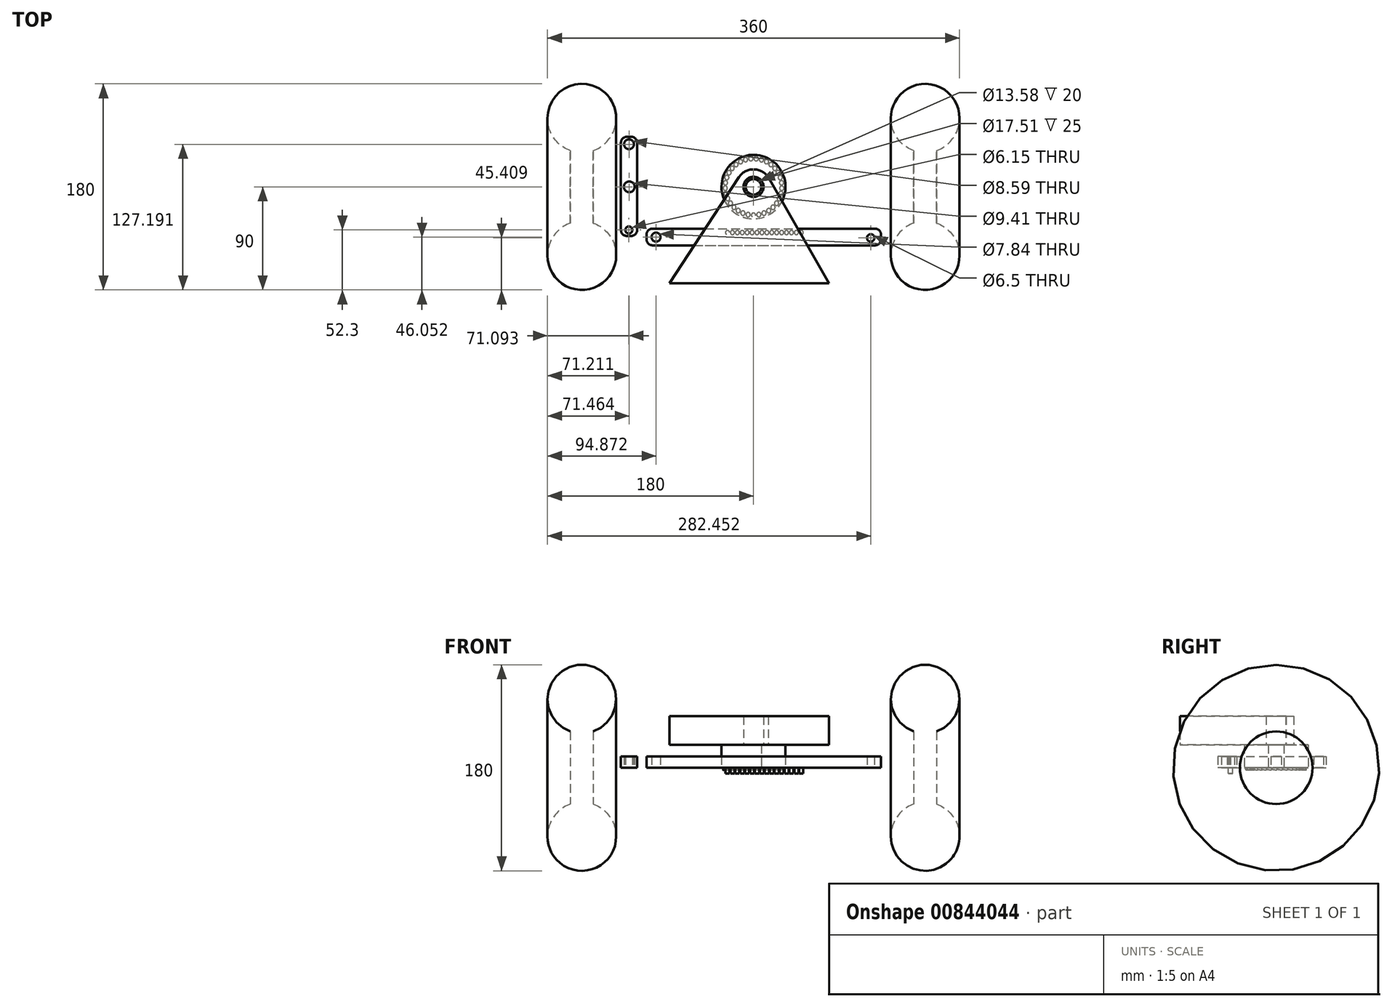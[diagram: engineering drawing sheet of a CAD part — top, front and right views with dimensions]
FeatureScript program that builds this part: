
annotation { "Feature Type Name" : "Feature", "Feature Type Description" : "" }
export const myFeature = defineFeature(function(context is Context, id is Id, definition is map)
    precondition{}
    {
        {
            var Q0;
            Q0=qCreatedBy(makeId("Front.planeOp"),FACE);
            var sketch = newSketch(context, id + "F0", { "sketchPlane" : qUnion([Q0])});
            skCircle(sketch, "E0", {"center": v(-150, 60) * mm, "radius": 30 * mm});
            skLineSegment(sketch, "E1.bottom", {"start": v(-160, 31.72) * mm, "end": v(-140, 31.72) * mm});
            skLineSegment(sketch, "E1.top", {"start": v(-160, 0) * mm, "end": v(-140, 0) * mm});
            skLineSegment(sketch, "E1.left", {"start": v(-140, 31.72) * mm, "end": v(-140, 0) * mm});
            skLineSegment(sketch, "E1.right", {"start": v(-160, 31.72) * mm, "end": v(-160, 0) * mm});
            skPoint(sketch, "E2.startSnap0", {"position": v(-150, 31.72) * mm});
            skLineSegment(sketch, "E3", {"start": v(-150, 31.72) * mm, "end": v(-150, 60) * mm});
            skLineSegment(sketch, "E4.MirrorCS", {"start": v(160, 31.72) * mm, "end": v(160, 0) * mm});
            skLineSegment(sketch, "E5.MirrorCS", {"start": v(140, 31.72) * mm, "end": v(140, 0) * mm});
            skPoint(sketch, "E6.MirrorP", {"position": v(150, 31.72) * mm});
            skLineSegment(sketch, "E7.MirrorCS", {"start": v(160, 31.72) * mm, "end": v(140, 31.72) * mm});
            skLineSegment(sketch, "E8.MirrorCS", {"start": v(160, 0) * mm, "end": v(140, 0) * mm});
            skCircle(sketch, "E9.MirrorC", {"center": v(150, 60) * mm, "radius": 30 * mm});
            skSolve(sketch);
        }
        {
            var Q0;
            Q0 = qSketchRegion(id + "F0", true);
            var Q1;
            Q1=sQuery(id+"F0.wireOp",EDGE,"E1.top");
            revolve(context, id + "F1", {"surfaceOperationType" : NewSurfaceOperationType.NEW, "entities" : qUnion([Q0]), "axis" : qUnion([Q1]), "revolveType" : RevolveType.FULL});
        }
        {
            var Q0;
            Q0=qCreatedBy(makeId("Top.planeOp"),FACE);
            var sketch = newSketch(context, id + "F2", { "sketchPlane" : qUnion([Q0])});
            skLineSegment(sketch, "E10.bottom", {"start": v(-110.82, -42.85) * mm, "end": v(-106.64, -42.85) * mm});
            skLineSegment(sketch, "E10.top", {"start": v(-110.82, 43.7) * mm, "end": v(-106.64, 43.7) * mm});
            skLineSegment(sketch, "E10.left", {"start": v(-115.82, -37.85) * mm, "end": v(-115.82, 38.7) * mm});
            skLineSegment(sketch, "E10.right", {"start": v(-101.64, -37.85) * mm, "end": v(-101.64, 38.7) * mm});
            skLineSegment(sketch, "E11.bottom", {"start": v(-88.44, -51.05) * mm, "end": v(106.34, -51.05) * mm});
            skLineSegment(sketch, "E11.top", {"start": v(-88.44, -36.5) * mm, "end": v(106.34, -36.5) * mm});
            skLineSegment(sketch, "E11.left", {"start": v(-93.44, -46.05) * mm, "end": v(-93.44, -41.5) * mm});
            skLineSegment(sketch, "E11.right", {"start": v(111.34, -46.05) * mm, "end": v(111.34, -41.5) * mm});
            skPoint(sketch, "E12.visualSharp", {"position": v(-93.44, -51.05) * mm});
            skArc(sketch, "E12.filletArc", {"start": v(-93.44, -46.05) * mm, "mid": v(-91.97, -49.59) * mm, "end": v(-88.44, -51.05) * mm});
            skPoint(sketch, "E13.visualSharp", {"position": v(-93.44, -36.5) * mm});
            skArc(sketch, "E13.filletArc", {"start": v(-88.44, -36.5) * mm, "mid": v(-91.97, -37.97) * mm, "end": v(-93.44, -41.5) * mm});
            skPoint(sketch, "E14.visualSharp", {"position": v(111.34, -51.05) * mm});
            skArc(sketch, "E14.filletArc", {"start": v(106.34, -51.05) * mm, "mid": v(109.88, -49.59) * mm, "end": v(111.34, -46.05) * mm});
            skPoint(sketch, "E15.visualSharp", {"position": v(111.34, -36.5) * mm});
            skArc(sketch, "E15.filletArc", {"start": v(111.34, -41.5) * mm, "mid": v(109.88, -37.97) * mm, "end": v(106.34, -36.5) * mm});
            skPoint(sketch, "E16.visualSharp", {"position": v(-101.64, -42.85) * mm});
            skArc(sketch, "E16.filletArc", {"start": v(-106.64, -42.85) * mm, "mid": v(-103.1, -41.38) * mm, "end": v(-101.64, -37.85) * mm});
            skPoint(sketch, "E17.visualSharp", {"position": v(-101.64, 43.7) * mm});
            skArc(sketch, "E17.filletArc", {"start": v(-101.64, 38.7) * mm, "mid": v(-103.1, 42.23) * mm, "end": v(-106.64, 43.7) * mm});
            skPoint(sketch, "E18.visualSharp", {"position": v(-115.82, 43.7) * mm});
            skArc(sketch, "E18.filletArc", {"start": v(-110.82, 43.7) * mm, "mid": v(-114.35, 42.23) * mm, "end": v(-115.82, 38.7) * mm});
            skPoint(sketch, "E19.visualSharp", {"position": v(-115.82, -42.85) * mm});
            skArc(sketch, "E19.filletArc", {"start": v(-115.82, -37.85) * mm, "mid": v(-114.35, -41.38) * mm, "end": v(-110.82, -42.85) * mm});
            skCircle(sketch, "E20", {"center": v(-85.13, -43.95) * mm, "radius": 3.92 * mm});
            skCircle(sketch, "E21", {"center": v(-108.9, -37.7) * mm, "radius": 3.08 * mm});
            skCircle(sketch, "E22", {"center": v(-108.79, 37.2) * mm, "radius": 4.3 * mm});
            skCircle(sketch, "E23", {"center": v(102.45, -44.6) * mm, "radius": 3.25 * mm});
            skCircle(sketch, "E24", {"center": v(-108.54, 0) * mm, "radius": 4.7 * mm});
            skSolve(sketch);
        }
        {
            var Q0;
            Q0 = qSketchRegion(id + "F2", true);
            extrude(context, id + "F3", {"entities" : qUnion([Q0]), "depth" : 10 * mm, "offsetDistance" : 25 * mm});
        }
        {
            var Q0;
            Q0=qCreatedBy(makeId("Top.planeOp"),FACE);
            var sketch = newSketch(context, id + "F4", { "sketchPlane" : qUnion([Q0])});
            skCircle(sketch, "E25", {"center": v(0, 0) * mm, "radius": 27.96 * mm});
            skCircle(sketch, "E26", {"center": v(0, 0) * mm, "radius": 6.79 * mm});
            skSolve(sketch);
        }
        {
            var Q0;
            Q0=makeQuery(id+"F4.imprint","IMPRINT",FACE,{"disambiguationData":[TD([[makeQuery(id+"F4.imprint","IMPRINT",EDGE,{"derivedFrom":sQuery(id+"F4.wireOp",EDGE,"E25")}),1.0]])]});
            extrude(context, id + "F5", {"entities" : qUnion([Q0]), "depth" : 20 * mm, "offsetDistance" : 25 * mm});
        }
        {
            var Q0;
            Q0=makeQuery(id+"F5.opExtrude","CAP_FACE",FACE,{"disambiguationData":[OSD([sQuery(id+"F4.wireOp",EDGE,"E25"),sQuery(id+"F4.wireOp",EDGE,"E26")])],"isStart":false});
            var sketch = newSketch(context, id + "F6", { "sketchPlane" : qUnion([Q0])});
            skLineSegment(sketch, "E27", {"start": v(-73.41, -84.14) * mm, "end": v(-12.8, 8.38) * mm});
            skLineSegment(sketch, "E28", {"start": v(12.8, 8.38) * mm, "end": v(66.1, -84.14) * mm});
            skArc(sketch, "E29", {"start": v(-12.8, 8.38) * mm, "mid": v(0, 15.3) * mm, "end": v(12.8, 8.38) * mm});
            skLineSegment(sketch, "E30", {"start": v(-73.41, -84.14) * mm, "end": v(66.1, -84.14) * mm});
            skCircle(sketch, "E31", {"center": v(0, 0) * mm, "radius": 8.76 * mm});
            skSolve(sketch);
        }
        {
            var Q0;
            Q0 = qSketchRegion(id + "F6", true);
            extrude(context, id + "F7", {"entities" : qUnion([Q0]), "operationType" : NewBodyOperationType.ADD, "depth" : 25 * mm, "offsetDistance" : 25 * mm});
        }
        {
            var Q0;
            Q0=makeQuery(id+"F5.opExtrude","CAP_FACE",FACE,{"disambiguationData":[OSD([sQuery(id+"F4.wireOp",EDGE,"E25"),sQuery(id+"F4.wireOp",EDGE,"E26")])],"isStart":true});
            var sketch = newSketch(context, id + "F8", { "sketchPlane" : qUnion([Q0])});
            skPoint(sketch, "E32.center", {"position": v(0, 0.62) * mm});
            skLineSegment(sketch, "E32.anchor1", {"start": v(0, 0.62) * mm, "end": v(0, 24.7) * mm, "construction": true});
            skPoint(sketch, "E33.center", {"position": v(8.35, 1.1) * mm});
            skCircle(sketch, "E34", {"center": v(0, 24.7) * mm, "radius": 1.9 * mm});
            skCircle(sketch, "E35.1.0", {"center": v(4.67, 24.26) * mm, "radius": 1.9 * mm});
            skCircle(sketch, "E35.2.0", {"center": v(9.18, 22.94) * mm, "radius": 1.9 * mm});
            skCircle(sketch, "E35.3.0", {"center": v(13.36, 20.79) * mm, "radius": 1.9 * mm});
            skCircle(sketch, "E35.4.0", {"center": v(17.05, 17.89) * mm, "radius": 1.9 * mm});
            skCircle(sketch, "E35.5.0", {"center": v(20.12, 14.34) * mm, "radius": 1.9 * mm});
            skCircle(sketch, "E35.6.0", {"center": v(22.47, 10.27) * mm, "radius": 1.9 * mm});
            skCircle(sketch, "E35.7.0", {"center": v(24.01, 5.83) * mm, "radius": 1.9 * mm});
            skCircle(sketch, "E35.8.0", {"center": v(24.68, 1.19) * mm, "radius": 1.9 * mm});
            skCircle(sketch, "E35.9.0", {"center": v(24.46, -3.5) * mm, "radius": 1.9 * mm});
            skCircle(sketch, "E35.10.0", {"center": v(23.35, -8.07) * mm, "radius": 1.9 * mm});
            skCircle(sketch, "E35.11.0", {"center": v(21.4, -12.34) * mm, "radius": 1.9 * mm});
            skCircle(sketch, "E35.12.0", {"center": v(18.68, -16.17) * mm, "radius": 1.9 * mm});
            skCircle(sketch, "E35.13.0", {"center": v(15.29, -19.41) * mm, "radius": 1.9 * mm});
            skCircle(sketch, "E35.14.0", {"center": v(11.34, -21.95) * mm, "radius": 1.9 * mm});
            skCircle(sketch, "E35.15.0", {"center": v(6.98, -23.7) * mm, "radius": 1.9 * mm});
            skCircle(sketch, "E35.16.0", {"center": v(2.37, -24.6) * mm, "radius": 1.9 * mm});
            skCircle(sketch, "E35.17.0", {"center": v(-2.33, -24.6) * mm, "radius": 1.9 * mm});
            skCircle(sketch, "E35.18.0", {"center": v(-6.94, -23.71) * mm, "radius": 1.9 * mm});
            skCircle(sketch, "E35.19.0", {"center": v(-11.3, -21.97) * mm, "radius": 1.9 * mm});
            skPoint(sketch, "E35.center", {"position": v(0, 0) * mm});
            skLineSegment(sketch, "E35.anchor1", {"start": v(0, 0) * mm, "end": v(0, 24.7) * mm, "construction": true});
            skLineSegment(sketch, "E35.anchor2", {"start": v(0, 0) * mm, "end": v(-4.71, 24.25) * mm, "construction": true});
            skCircle(sketch, "E36.1.20.0", {"center": v(-15.25, -19.44) * mm, "radius": 1.9 * mm});
            skCircle(sketch, "E37.1.21.0", {"center": v(-18.66, -16.2) * mm, "radius": 1.9 * mm});
            skCircle(sketch, "E38.1.22.0", {"center": v(-21.38, -12.38) * mm, "radius": 1.9 * mm});
            skCircle(sketch, "E39.1.23.0", {"center": v(-23.34, -8.1) * mm, "radius": 1.9 * mm});
            skCircle(sketch, "E40.1.24.0", {"center": v(-24.45, -3.55) * mm, "radius": 1.9 * mm});
            skCircle(sketch, "E41.1.25.0", {"center": v(-24.68, 1.15) * mm, "radius": 1.9 * mm});
            skCircle(sketch, "E42.1.26.0", {"center": v(-24.02, 5.8) * mm, "radius": 1.9 * mm});
            skCircle(sketch, "E43.1.27.0", {"center": v(-22.49, 10.23) * mm, "radius": 1.9 * mm});
            skCircle(sketch, "E44.1.28.0", {"center": v(-20.15, 14.3) * mm, "radius": 1.9 * mm});
            skCircle(sketch, "E45.1.29.0", {"center": v(-17.08, 17.86) * mm, "radius": 1.9 * mm});
            skCircle(sketch, "E46.1.30.0", {"center": v(-13.39, 20.77) * mm, "radius": 1.9 * mm});
            skCircle(sketch, "E47.1.31.0", {"center": v(-9.22, 22.92) * mm, "radius": 1.9 * mm});
            skCircle(sketch, "E48.1.32.0", {"center": v(-4.71, 24.25) * mm, "radius": 1.9 * mm});
            skSolve(sketch);
        }
        {
            var Q0;
            Q0=makeQuery(id+"F3.opExtrude","CAP_FACE",FACE,{"disambiguationData":[OSD([sQuery(id+"F2.wireOp",EDGE,"E11.bottom"),sQuery(id+"F2.wireOp",EDGE,"E11.top"),sQuery(id+"F2.wireOp",EDGE,"E11.left"),sQuery(id+"F2.wireOp",EDGE,"E11.right"),sQuery(id+"F2.wireOp",EDGE,"E12.filletArc"),sQuery(id+"F2.wireOp",EDGE,"E13.filletArc"),sQuery(id+"F2.wireOp",EDGE,"E14.filletArc"),sQuery(id+"F2.wireOp",EDGE,"E15.filletArc"),sQuery(id+"F2.wireOp",EDGE,"E20"),sQuery(id+"F2.wireOp",EDGE,"E23")])],"isStart":true});
            var sketch = newSketch(context, id + "F9", { "sketchPlane" : qUnion([Q0])});
            skPoint(sketch, "E49", {"position": v(8.95, 36.5) * mm});
            skCircle(sketch, "E50", {"center": v(-22.74, 39.93) * mm, "radius": 1.78 * mm});
            skCircle(sketch, "E51.1.0.0", {"center": v(-18.44, 39.93) * mm, "radius": 1.78 * mm});
            skCircle(sketch, "E51.2.0.0", {"center": v(-14.14, 39.93) * mm, "radius": 1.78 * mm});
            skCircle(sketch, "E51.3.0.0", {"center": v(-9.84, 39.93) * mm, "radius": 1.78 * mm});
            skCircle(sketch, "E51.4.0.0", {"center": v(-5.54, 39.93) * mm, "radius": 1.78 * mm});
            skCircle(sketch, "E51.5.0.0", {"center": v(-1.24, 39.93) * mm, "radius": 1.78 * mm});
            skCircle(sketch, "E51.6.0.0", {"center": v(3.06, 39.93) * mm, "radius": 1.78 * mm});
            skCircle(sketch, "E51.7.0.0", {"center": v(7.36, 39.93) * mm, "radius": 1.78 * mm});
            skCircle(sketch, "E51.8.0.0", {"center": v(11.66, 39.93) * mm, "radius": 1.78 * mm});
            skCircle(sketch, "E51.9.0.0", {"center": v(15.96, 39.93) * mm, "radius": 1.78 * mm});
            skCircle(sketch, "E51.10.0.0", {"center": v(20.26, 39.93) * mm, "radius": 1.78 * mm});
            skCircle(sketch, "E51.11.0.0", {"center": v(24.56, 39.93) * mm, "radius": 1.78 * mm});
            skCircle(sketch, "E51.12.0.0", {"center": v(28.86, 39.93) * mm, "radius": 1.78 * mm});
            skCircle(sketch, "E51.13.0.0", {"center": v(33.16, 39.93) * mm, "radius": 1.78 * mm});
            skCircle(sketch, "E51.14.0.0", {"center": v(37.46, 39.93) * mm, "radius": 1.78 * mm});
            skCircle(sketch, "E51.15.0.0", {"center": v(41.76, 39.93) * mm, "radius": 1.78 * mm});
            skLineSegment(sketch, "E51.direction1", {"start": v(-22.74, 39.93) * mm, "end": v(-18.44, 39.93) * mm, "construction": true});
            skSolve(sketch);
        }
        {
            var Q0;
            Q0 = qSketchRegion(id + "F8", true);
            extrude(context, id + "F10", {"entities" : qUnion([Q0]), "operationType" : NewBodyOperationType.ADD, "depth" : 2 * mm, "offsetDistance" : 25 * mm});
        }
        {
            var Q0;
            Q0 = qSketchRegion(id + "F9", true);
            extrude(context, id + "F11", {"entities" : qUnion([Q0]), "operationType" : NewBodyOperationType.ADD, "depth" : 5 * mm, "offsetDistance" : 25 * mm});
        }
    });
